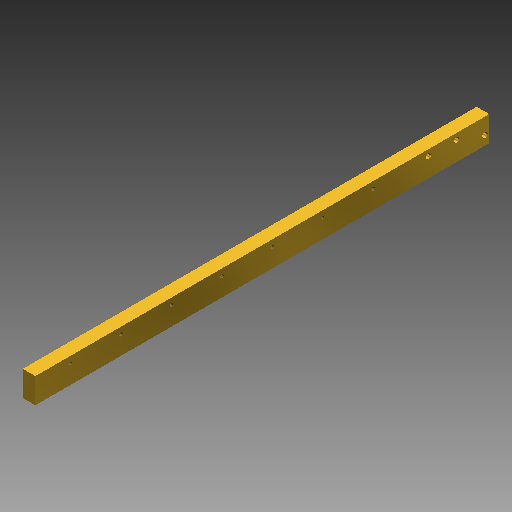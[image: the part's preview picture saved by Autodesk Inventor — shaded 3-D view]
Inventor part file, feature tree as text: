
AUTODESK INVENTOR PART (.ipt)
format: ipt  version: 2017 (Build 210142000, 142)  size: 145,408 bytes
history: native  units: in
note: dims shown in document units (in); Inventor stores cm internally (conversion verified against a paired STEP export)
features: hole x4, pattern_linear x4, sketch x3, extrude x1
ambient origin geometry x8: Origin, YZ Plane, XZ Plane, XY Plane, X Axis, Y Axis, Z Axis, Center Point
bodies: Solid1 (feature_tree)
feature tree (12):
  extrude  "Extrusion1"  Depth=0.5in
  sketch  "Sketch3"  dims[d6=9.0in d7=0.0in d8=0.1344in]
  hole  "Hole1"  [1 undecoded]
  pattern_linear  "Rectangular Pattern1"  Count1=7 Spacing1=1.0in
  sketch  "Sketch6"  dims[d9=0.7in d10=0.067in d11=0.75in d12=0.375in d13=0.25in d14=0.5635in d15=1.0in d16=0.8108in d17=2.7559in d19=1.0in d20=0.75in d23=0.8108in d24=0.5635in d25=0.25in d26=0.375in d27=0.25in d28=0.067in d45=7.793in d46=0.121in d47=0.109in d48=0.75in d49=0.375in d50=0.25in d51=0.5635in d52=0.26in d53=0.8108in d54=1.1811in d56=0.561in d57=0.7874in d59=0.197in d61=0.067in d62=0.75in d63=0.375in d64=0.25in d65=0.5635in d66=0.25in d67=0.8108in d68=2.3in d69=0.15in d70=0.7874in d72=1.0in d73=1.9685in d75=1.5in d76=0.125in d77=0.125in]
  hole  "Hole4"  [1 undecoded]
  pattern_linear  "Rectangular Pattern4"  Spacing1=7.793in  [1 undecoded]
  hole  "Hole5"  [1 undecoded]
  pattern_linear  "Rectangular Pattern5"  Count1=3 Spacing1=0.561in
  pattern_linear  "Rectangular Pattern6"  Spacing1=2.3in  [1 undecoded]
  sketch  "Sketch2"  dims[d3=0.25in d5=0.5in]
  hole  "Hole2"  [1 undecoded]
note: 6 required parameter values undecoded (feature->parameter linkage not recoverable at this tier; creation-order binding heuristic only, values carry confidence <= 0.55)
